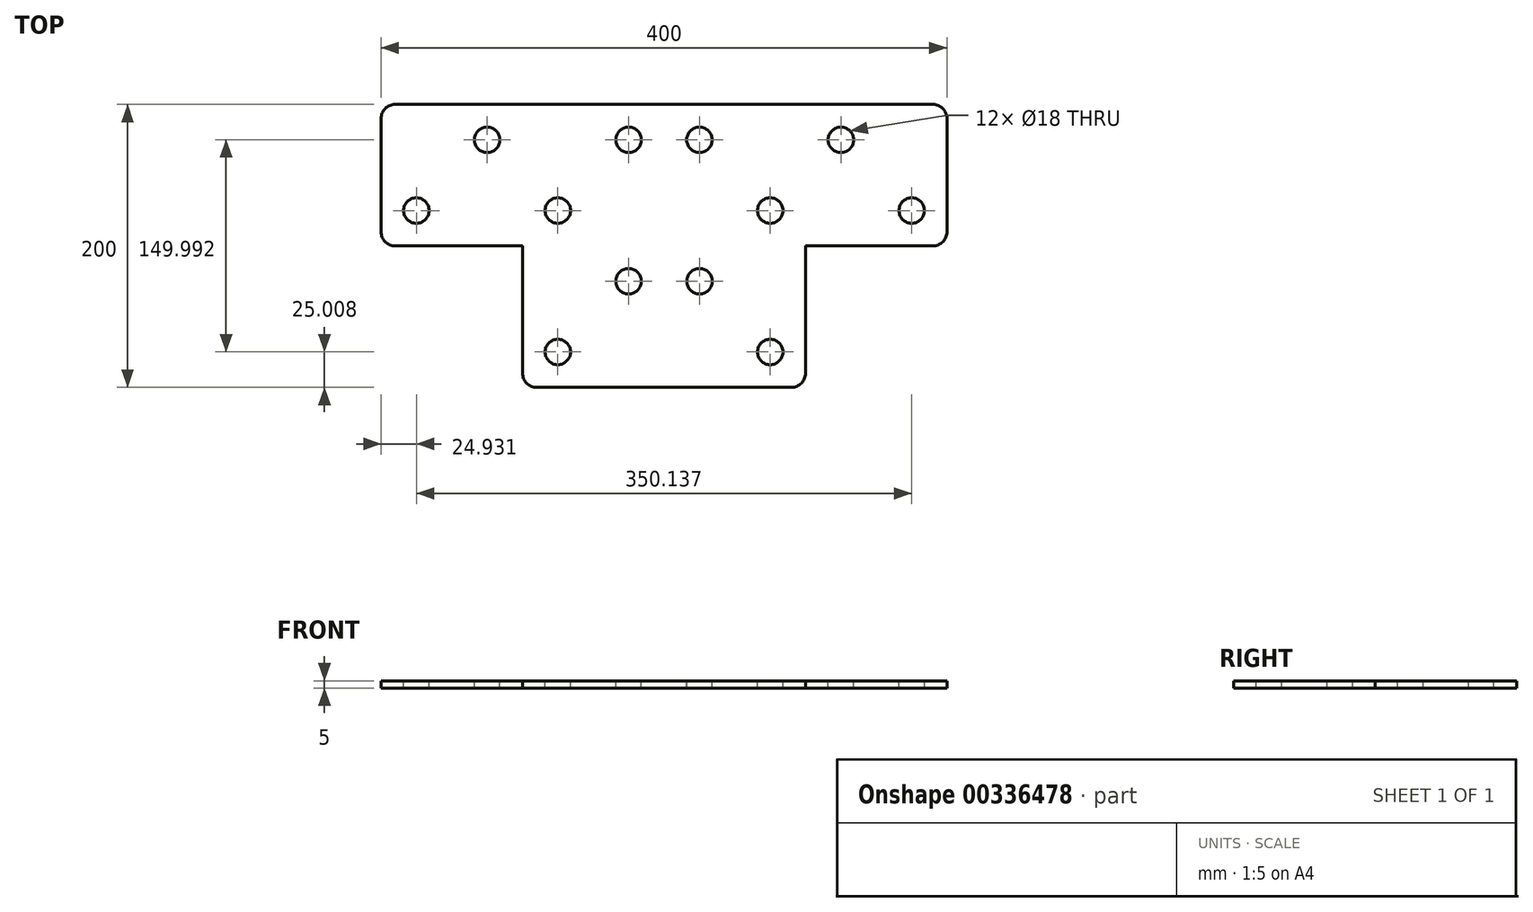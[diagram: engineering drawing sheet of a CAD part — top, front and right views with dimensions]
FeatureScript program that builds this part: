
annotation { "Feature Type Name" : "Feature", "Feature Type Description" : "" }
export const myFeature = defineFeature(function(context is Context, id is Id, definition is map)
    precondition{}
    {
        {
            var Q0;
            Q0=qCreatedBy(makeId("Top.planeOp"),FACE);
            var sketch = newSketch(context, id + "F0", { "sketchPlane" : qUnion([Q0])});
            skLineSegment(sketch, "E0", {"start": v(0, 0) * mm, "end": v(200, 0) * mm});
            skLineSegment(sketch, "E1", {"start": v(200, 0) * mm, "end": v(200, -100) * mm});
            skLineSegment(sketch, "E2", {"start": v(200, -100) * mm, "end": v(100, -100) * mm});
            skLineSegment(sketch, "E3", {"start": v(100, -100) * mm, "end": v(100, -200) * mm});
            skLineSegment(sketch, "E4", {"start": v(100, -200) * mm, "end": v(0, -200) * mm});
            skLineSegment(sketch, "E5.MirrorCS", {"start": v(0, 0) * mm, "end": v(-200, 0) * mm});
            skLineSegment(sketch, "E6.MirrorCS", {"start": v(-200, 0) * mm, "end": v(-200, -100) * mm});
            skLineSegment(sketch, "E7.MirrorCS", {"start": v(-200, -100) * mm, "end": v(-100, -100) * mm});
            skLineSegment(sketch, "E8.MirrorCS", {"start": v(-100, -100) * mm, "end": v(-100, -200) * mm});
            skLineSegment(sketch, "E9.MirrorCS", {"start": v(-100, -200) * mm, "end": v(0, -200) * mm});
            skSolve(sketch);
        }
        {
            var Q0;
            Q0=makeQuery(id+"F0.imprint","IMPRINT",FACE,{"disambiguationData":[TD([[makeQuery(id+"F0.imprint","IMPRINT",EDGE,{"derivedFrom":sQuery(id+"F0.wireOp",EDGE,"E0")}),-1.0]])]});
            extrude(context, id + "F1", {"entities" : qUnion([Q0]), "depth" : 5 * mm});
        }
        {
            var Q0;
            Q0=makeQuery(id+"F1.opExtrude","CAP_FACE",FACE,{"disambiguationData":[OSD([sQuery(id+"F0.wireOp",EDGE,"E0"),sQuery(id+"F0.wireOp",EDGE,"E1"),sQuery(id+"F0.wireOp",EDGE,"E2"),sQuery(id+"F0.wireOp",EDGE,"E3"),sQuery(id+"F0.wireOp",EDGE,"E4"),sQuery(id+"F0.wireOp",EDGE,"E5.MirrorCS"),sQuery(id+"F0.wireOp",EDGE,"E6.MirrorCS"),sQuery(id+"F0.wireOp",EDGE,"E7.MirrorCS"),sQuery(id+"F0.wireOp",EDGE,"E8.MirrorCS"),sQuery(id+"F0.wireOp",EDGE,"E9.MirrorCS")])],"isStart":false});
            var sketch = newSketch(context, id + "F2", { "sketchPlane" : qUnion([Q0])});
            skPoint(sketch, "E10.startSnap0", {"position": v(175.07, -50) * mm});
            skCircle(sketch, "E11.MirrorC", {"center": v(175.07, -75) * mm, "radius": 9 * mm});
            skCircle(sketch, "E12.MirrorC", {"center": v(125, -25) * mm, "radius": 9 * mm});
            skCircle(sketch, "E13.MirrorC", {"center": v(75.07, -75) * mm, "radius": 9 * mm});
            skCircle(sketch, "E14.MirrorC", {"center": v(75.07, -175) * mm, "radius": 9 * mm});
            skCircle(sketch, "E15.MirrorC", {"center": v(25.07, -125) * mm, "radius": 9 * mm});
            skCircle(sketch, "E16.MirrorC", {"center": v(25, -25) * mm, "radius": 9 * mm});
            skPoint(sketch, "E17.MirrorP", {"position": v(-175.07, -50) * mm});
            skCircle(sketch, "E18.MirrorC", {"center": v(-75.07, -175) * mm, "radius": 9 * mm});
            skCircle(sketch, "E19.MirrorC", {"center": v(-25, -25) * mm, "radius": 9 * mm});
            skCircle(sketch, "E20.MirrorC", {"center": v(-175.07, -75) * mm, "radius": 9 * mm});
            skCircle(sketch, "E21.MirrorC", {"center": v(-125, -25) * mm, "radius": 9 * mm});
            skCircle(sketch, "E22.MirrorC", {"center": v(-75.07, -75) * mm, "radius": 9 * mm});
            skCircle(sketch, "E23.MirrorC", {"center": v(-25.07, -125) * mm, "radius": 9 * mm});
            skSolve(sketch);
        }
        {
            var Q0;
            Q0 = qSketchRegion(id + "F2", true);
            extrude(context, id + "F3", {"entities" : qUnion([Q0]), "operationType" : NewBodyOperationType.REMOVE, "oppositeDirection" : true, "depth" : 25 * mm});
        }
        {
            var Q0;
            Q0=makeQuery(id+"F1.opExtrude","SWEPT_EDGE",EDGE,{"disambiguationData":[OSD([sQuery(id+"F0.wireOp",EDGE,"E8.MirrorCS"),sQuery(id+"F0.wireOp",EDGE,"E9.MirrorCS")])]});
            var Q1;
            Q1=makeQuery(id+"F1.opExtrude","SWEPT_EDGE",EDGE,{"disambiguationData":[OSD([sQuery(id+"F0.wireOp",EDGE,"E3"),sQuery(id+"F0.wireOp",EDGE,"E4")])]});
            var Q2;
            Q2=makeQuery(id+"F1.opExtrude","SWEPT_EDGE",EDGE,{"disambiguationData":[OSD([sQuery(id+"F0.wireOp",EDGE,"E1"),sQuery(id+"F0.wireOp",EDGE,"E2")])]});
            var Q3;
            Q3=makeQuery(id+"F1.opExtrude","SWEPT_EDGE",EDGE,{"disambiguationData":[OSD([sQuery(id+"F0.wireOp",EDGE,"E0"),sQuery(id+"F0.wireOp",EDGE,"E1")])]});
            var Q4;
            Q4=makeQuery(id+"F1.opExtrude","SWEPT_EDGE",EDGE,{"disambiguationData":[OSD([sQuery(id+"F0.wireOp",EDGE,"E6.MirrorCS"),sQuery(id+"F0.wireOp",EDGE,"E7.MirrorCS")])]});
            var Q5;
            Q5=makeQuery(id+"F1.opExtrude","SWEPT_EDGE",EDGE,{"disambiguationData":[OSD([sQuery(id+"F0.wireOp",EDGE,"E5.MirrorCS"),sQuery(id+"F0.wireOp",EDGE,"E6.MirrorCS")])]});
            fillet(context, id + "F4", {"entities" : qUnion([Q0, Q1, Q2, Q3, Q4, Q5]), "radius" : 10 * mm, "tangentPropagation" : true, "allowEdgeOverflow" : false});
        }
    });
